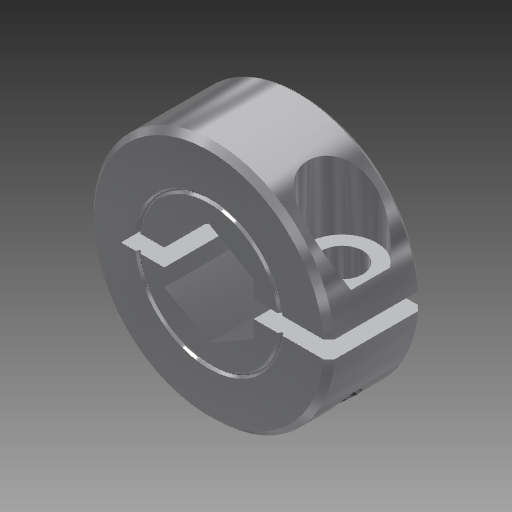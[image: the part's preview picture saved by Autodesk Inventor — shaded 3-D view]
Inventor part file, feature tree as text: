
AUTODESK INVENTOR PART (.ipt)
format: ipt  version: 2017.1 (Build 211199000, 199)  size: 465,408 bytes
history: native  units: mm
features: sketch x6, extrude x4, hole x2, other x2, surface_op x1, thread x1, projected_geometry x1
ambient origin geometry x8: Origin, YZ Plane, XZ Plane, XY Plane, X Axis, Y Axis, Z Axis, Center Point
bodies: Solid1 (feature_tree)
feature tree (17):
  surface_op  "Stitch Surface1"
  thread  "Thread1"  [1 undecoded]
  hole  "Hole1"  [1 undecoded]
  extrude  "Extrusion1"  Depth=10.0mm TaperAngle=0.0deg
  hole  "Hole2"  [1 undecoded]
  extrude  "Extrusion2"  [1 undecoded]
  extrude  "Extrusion3"  [1 undecoded]
  extrude  "Extrusion4"  [1 undecoded]
  sketch  "Sketch1"  dims[d2=3.797mm d3=6.0mm d4=12.7mm d5=2.362mm d6=14.3117mm d7=8.0mm d8=20.594885mm d9=9.25mm d10=0.0mm]
  sketch  "Sketch2"  dims[d11=2.642mm d12=10.0mm d13=12.7mm d14=2.362mm d15=14.3117mm d16=8.0mm d17=20.594885mm d18=8.5mm d19=0.0mm]
  sketch  "Sketch3"  dims[d20=9.525mm d21=10.0mm d22=0.0mm]
  projected_geometry  "Projected Loop1"
  sketch  "Sketch4"  dims[d23=10.0mm d24=0.0mm]
  sketch  "Sketch5"
  sketch  "Sketch6"
  other  "Composite1"
  other  "Srf1"
note: 6 required parameter values undecoded (feature->parameter linkage not recoverable at this tier; creation-order binding heuristic only, values carry confidence <= 0.55)
